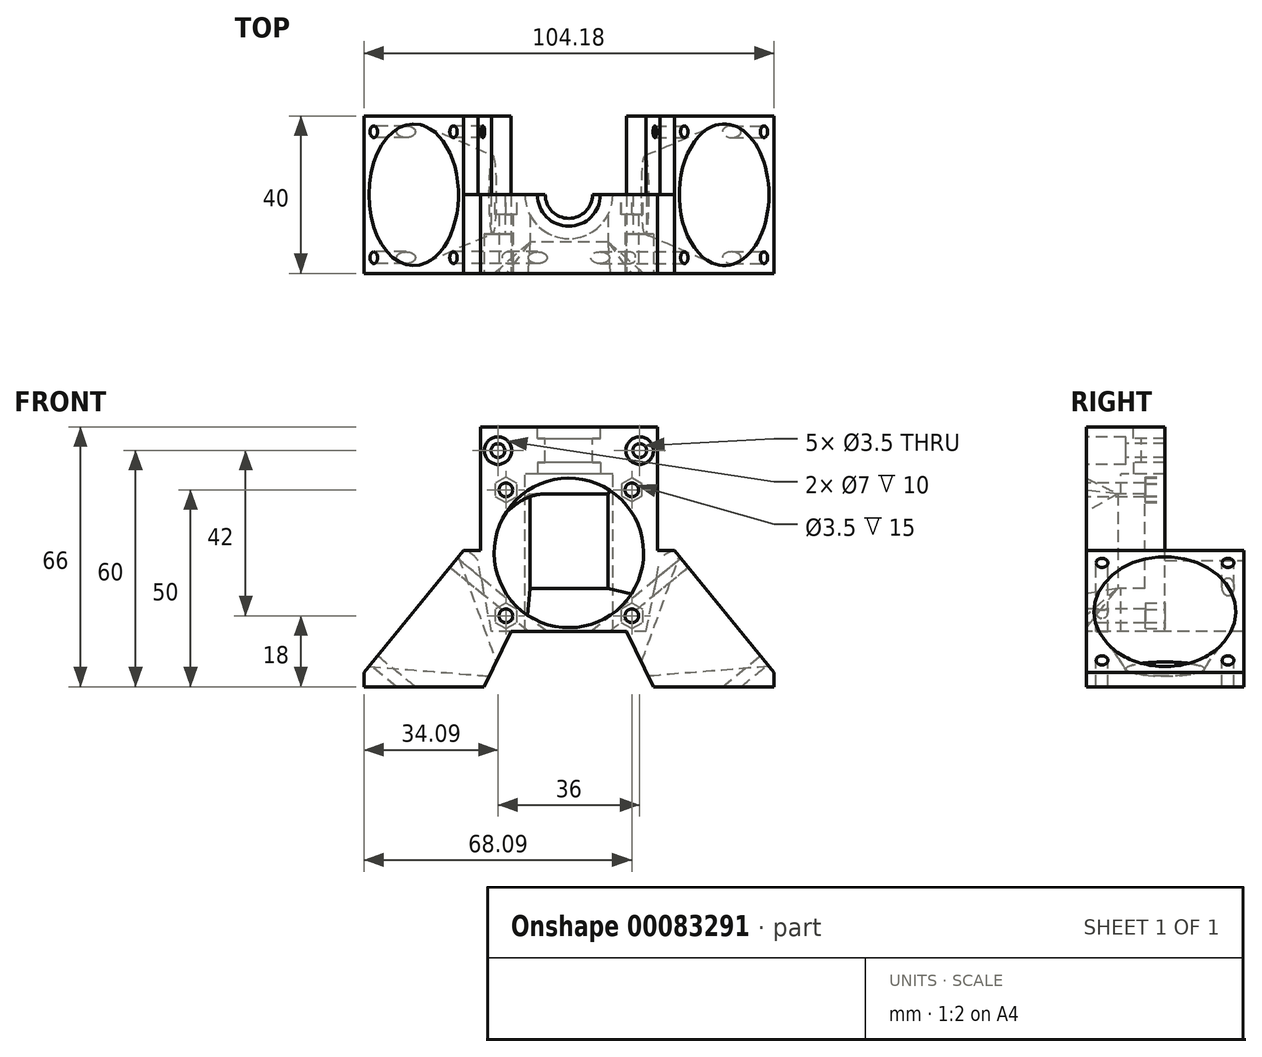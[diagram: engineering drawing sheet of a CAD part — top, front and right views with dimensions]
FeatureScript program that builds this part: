
annotation { "Feature Type Name" : "Feature", "Feature Type Description" : "" }
export const myFeature = defineFeature(function(context is Context, id is Id, definition is map)
    precondition{}
    {
        {
            var Q0;
            Q0=qCreatedBy(makeId("Front.planeOp"),FACE);
            var sketch = newSketch(context, id + "F0", { "sketchPlane" : qUnion([Q0])});
            skLineSegment(sketch, "E0.bottom", {"start": v(22.5, 6) * mm, "end": v(-22.5, 6) * mm});
            skLineSegment(sketch, "E0.top", {"start": v(22.5, -6) * mm, "end": v(-22.5, -6) * mm});
            skLineSegment(sketch, "E0.left", {"start": v(22.5, 6) * mm, "end": v(22.5, -6) * mm});
            skLineSegment(sketch, "E0.right", {"start": v(-22.5, 6) * mm, "end": v(-22.5, -6) * mm});
            skPoint(sketch, "E0.middle", {"position": v(0, 0) * mm});
            skCircle(sketch, "E1", {"center": v(-18, 0) * mm, "radius": 1.75 * mm});
            skCircle(sketch, "E2", {"center": v(-18, 0) * mm, "radius": 3.5 * mm});
            skCircle(sketch, "E3", {"center": v(18, 0) * mm, "radius": 1.75 * mm});
            skCircle(sketch, "E4", {"center": v(18, 0) * mm, "radius": 3.5 * mm});
            skSolve(sketch);
        }
        {
            var Q0;
            Q0=qSketchRegion(id+"F0",true);
            var Q1;
            Q1=makeQuery(id+"F0.imprint","IMPRINT",FACE,{"disambiguationData":[TD([[makeQuery(id+"F0.imprint","IMPRINT",EDGE,{"derivedFrom":sQuery(id+"F0.wireOp",EDGE,"E1")}),-1.0]])]});
            var Q2;
            Q2=makeQuery(id+"F0.imprint","IMPRINT",FACE,{"disambiguationData":[TD([[makeQuery(id+"F0.imprint","IMPRINT",EDGE,{"derivedFrom":sQuery(id+"F0.wireOp",EDGE,"E3")}),-1.0]])]});
            extrude(context, id + "F1", {"entities" : qUnion([Q0, Q1, Q2]), "oppositeDirection" : true, "depth" : 20 * mm});
        }
        {
            var Q0;
            Q0=makeQuery(id+"F0.imprint","IMPRINT",FACE,{"disambiguationData":[TD([[makeQuery(id+"F0.imprint","IMPRINT",EDGE,{"derivedFrom":sQuery(id+"F0.wireOp",EDGE,"E1")}),-1.0]])]});
            var Q1;
            Q1=makeQuery(id+"F0.imprint","IMPRINT",FACE,{"disambiguationData":[TD([[makeQuery(id+"F0.imprint","IMPRINT",EDGE,{"derivedFrom":sQuery(id+"F0.wireOp",EDGE,"E3")}),-1.0]])]});
            extrude(context, id + "F2", {"entities" : qUnion([Q0, Q1]), "operationType" : NewBodyOperationType.REMOVE, "oppositeDirection" : true, "depth" : 10 * mm});
        }
        {
            var Q0;
            Q0=makeQuery(id+"F1.opExtrude","SWEPT_FACE",FACE,{"disambiguationData":[OSD([sQuery(id+"F0.wireOp",EDGE,"E0.bottom")])]});
            var sketch = newSketch(context, id + "F3", { "sketchPlane" : qUnion([Q0])});
            skCircle(sketch, "E5", {"center": v(0, 20) * mm, "radius": 6 * mm});
            skCircle(sketch, "E6", {"center": v(0, 20) * mm, "radius": 8 * mm});
            skSolve(sketch);
        }
        {
            var Q0;
            {var subQ0=sQuery(id+"F3.wireOp",EDGE,"E5");var subQ1=makeQuery(id+"F1.opExtrude","CAP_EDGE",EDGE,{"disambiguationData":[OSD([sQuery(id+"F0.wireOp",EDGE,"E0.bottom")])],"isStart":false});var subQ2=makeQuery(id+"F3.imprint","INTERSECT",VERTEX,{"disambiguationData":[OD(0.0)],"derivedFrom":[subQ1,subQ0]});Q0=makeQuery(id+"F3.imprint","IMPRINT",FACE,{"disambiguationData":[TD([[makeQuery(id+"F3.imprint","IMPRINT",EDGE,{"disambiguationData":[TD([[subQ2,-1.0]])],"derivedFrom":subQ0}),-1.0]])]});}
            var Q1;
            {var subQ0=sQuery(id+"F3.wireOp",EDGE,"E5");var subQ1=makeQuery(id+"F1.opExtrude","CAP_EDGE",EDGE,{"disambiguationData":[OSD([sQuery(id+"F0.wireOp",EDGE,"E0.bottom")])],"isStart":false});var subQ2=makeQuery(id+"F3.imprint","INTERSECT",VERTEX,{"disambiguationData":[OD(0.0)],"derivedFrom":[subQ1,subQ0]});Q1=makeQuery(id+"F3.imprint","IMPRINT",FACE,{"disambiguationData":[TD([[makeQuery(id+"F3.imprint","IMPRINT",EDGE,{"disambiguationData":[TD([[subQ2,-1.0]])],"derivedFrom":subQ0}),1.0]])]});}
            var Q2;
            {var subQ0=sQuery(id+"F3.wireOp",EDGE,"E5");var subQ1=makeQuery(id+"F1.opExtrude","CAP_EDGE",EDGE,{"disambiguationData":[OSD([sQuery(id+"F0.wireOp",EDGE,"E0.bottom")])],"isStart":false});var subQ2=makeQuery(id+"F3.imprint","INTERSECT",VERTEX,{"disambiguationData":[OD(0.0)],"derivedFrom":[subQ1,subQ0]});Q2=makeQuery(id+"F3.imprint","IMPRINT",FACE,{"disambiguationData":[TD([[makeQuery(id+"F3.imprint","IMPRINT",EDGE,{"disambiguationData":[TD([[subQ2,1.0]])],"derivedFrom":subQ0}),1.0]])]});}
            extrude(context, id + "F4", {"entities" : qUnion([Q0, Q1, Q2]), "operationType" : NewBodyOperationType.REMOVE, "endBound" : BoundingType.THROUGH_ALL, "oppositeDirection" : true, "depth" : 25 * mm});
        }
        {
            var Q0;
            Q0=qSketchRegion(id+"F3",true);
            extrude(context, id + "F5", {"entities" : qUnion([Q0]), "operationType" : NewBodyOperationType.REMOVE, "oppositeDirection" : true, "depth" : 3 * mm});
        }
        {
            var Q0;
            Q0=makeQuery(id+"F1.opExtrude","SWEPT_FACE",FACE,{"disambiguationData":[OSD([sQuery(id+"F0.wireOp",EDGE,"E0.top")])]});
            var sketch = newSketch(context, id + "F6", { "sketchPlane" : qUnion([Q0])});
            skCircle(sketch, "E7", {"center": v(0, -20) * mm, "radius": 8 * mm});
            skSolve(sketch);
        }
        {
            var Q0;
            Q0=qSketchRegion(id+"F6",true);
            extrude(context, id + "F7", {"entities" : qUnion([Q0]), "operationType" : NewBodyOperationType.REMOVE, "oppositeDirection" : true, "depth" : 3 * mm});
        }
        {
            var Q0;
            {var subQ0=sQuery(id+"F0.wireOp",EDGE,"E0.top");Q0=makeQuery(id+"F6.imprint","IMPRINT",FACE,{"disambiguationData":[TD([[makeQuery(id+"F6.imprint","IMPRINT",EDGE,{"derivedFrom":makeQuery(id+"F1.opExtrude","CAP_EDGE",EDGE,{"disambiguationData":[OSD([subQ0])],"isStart":true})}),1.0]])]});}
            var sketch = newSketch(context, id + "F8", { "sketchPlane" : qUnion([Q0])});
            skLineSegment(sketch, "E8.bottom", {"start": v(-22.5, 0) * mm, "end": v(22.5, 0) * mm});
            skLineSegment(sketch, "E8.top", {"start": v(-22.5, -20) * mm, "end": v(-11.15, -20) * mm});
            skLineSegment(sketch, "E8.left", {"start": v(-22.5, 0) * mm, "end": v(-22.5, -20) * mm});
            skLineSegment(sketch, "E8.right", {"start": v(22.5, 0) * mm, "end": v(22.5, -20) * mm});
            skArc(sketch, "E9", {"start": v(11.15, -20) * mm, "mid": v(0, -8.85) * mm, "end": v(-11.15, -20) * mm});
            skLineSegment(sketch, "E10.trimOffspring", {"start": v(11.15, -20) * mm, "end": v(22.5, -20) * mm});
            skSolve(sketch);
        }
        {
            var Q0;
            Q0 = qSketchRegion(id + "F8", true);
            extrude(context, id + "F9", {"entities" : qUnion([Q0]), "operationType" : NewBodyOperationType.ADD, "depth" : 40 * mm});
        }
        {
            var Q0;
            Q0=makeQuery(id+"F9.boolean.opBoolean","MERGE",FACE,{"derivedFrom":[makeQuery(id+"F1.opExtrude","CAP_FACE",FACE,{"disambiguationData":[OSD([sQuery(id+"F0.wireOp",EDGE,"E0.bottom"),sQuery(id+"F0.wireOp",EDGE,"E0.top"),sQuery(id+"F0.wireOp",EDGE,"E0.left"),sQuery(id+"F0.wireOp",EDGE,"E0.right"),sQuery(id+"F0.wireOp",EDGE,"E1"),sQuery(id+"F0.wireOp",EDGE,"E3")])],"isStart":true}),makeQuery(id+"F9.opExtrude","SWEPT_FACE",FACE,{"disambiguationData":[OSD([sQuery(id+"F8.wireOp",EDGE,"E8.bottom")])]})]});
            cPlane(context, id + "F10", {"entities" : qUnion([Q0]), "cplaneType" : CPlaneType.OFFSET, "offset" : 8 * mm, "oppositeDirection" : true, "width" : 150 * mm, "height" : 150 * mm});
        }
        {
            var Q0;
            Q0=qCreatedBy(id+"F10.planeOp",FACE);
            var sketch = newSketch(context, id + "F11", { "sketchPlane" : qUnion([Q0])});
            skLineSegment(sketch, "E11.bottom", {"start": v(9.89, -11) * mm, "end": v(-9.89, -11) * mm});
            skLineSegment(sketch, "E11.top", {"start": v(9.89, -35) * mm, "end": v(-9.89, -35) * mm});
            skLineSegment(sketch, "E11.left", {"start": v(9.89, -11) * mm, "end": v(9.89, -35) * mm});
            skLineSegment(sketch, "E11.right", {"start": v(-9.89, -11) * mm, "end": v(-9.89, -35) * mm});
            skPoint(sketch, "E11.middle", {"position": v(0, -23) * mm});
            skSolve(sketch);
        }
        {
            var Q0;
            Q0=makeQuery(id+"F9.boolean.opBoolean","MERGE",FACE,{"derivedFrom":[makeQuery(id+"F1.opExtrude","CAP_FACE",FACE,{"disambiguationData":[OSD([sQuery(id+"F0.wireOp",EDGE,"E0.bottom"),sQuery(id+"F0.wireOp",EDGE,"E0.top"),sQuery(id+"F0.wireOp",EDGE,"E0.left"),sQuery(id+"F0.wireOp",EDGE,"E0.right"),sQuery(id+"F0.wireOp",EDGE,"E1"),sQuery(id+"F0.wireOp",EDGE,"E3")])],"isStart":true}),makeQuery(id+"F9.opExtrude","SWEPT_FACE",FACE,{"disambiguationData":[OSD([sQuery(id+"F8.wireOp",EDGE,"E8.bottom")])]})]});
            var sketch = newSketch(context, id + "F12", { "sketchPlane" : qUnion([Q0])});
            skCircle(sketch, "E12", {"center": v(0, -26) * mm, "radius": 19 * mm});
            skSolve(sketch);
        }
        {
            var Q1;
            Q1 = qSketchRegion(id + "F11", true);
            var Q2;
            Q2 = qSketchRegion(id + "F12", true);
            loft(context, id + "F13", {"operationType" : NewBodyOperationType.REMOVE, "sheetProfilesArray" : [{ "sheetProfileEntities" : qUnion([Q1]) }, { "sheetProfileEntities" : qUnion([Q2]) }]});
        }
        {
            var Q0;
            Q0 = qSketchRegion(id + "F11", true);
            extrude(context, id + "F14", {"entities" : qUnion([Q0]), "operationType" : NewBodyOperationType.REMOVE, "endBound" : BoundingType.THROUGH_ALL, "oppositeDirection" : true, "depth" : 25 * mm});
        }
        {
            var Q0;
            Q0=makeQuery(id+"F9.boolean.opBoolean","MERGE",FACE,{"derivedFrom":[makeQuery(id+"F1.opExtrude","CAP_FACE",FACE,{"disambiguationData":[OSD([sQuery(id+"F0.wireOp",EDGE,"E0.bottom"),sQuery(id+"F0.wireOp",EDGE,"E0.top"),sQuery(id+"F0.wireOp",EDGE,"E0.left"),sQuery(id+"F0.wireOp",EDGE,"E0.right"),sQuery(id+"F0.wireOp",EDGE,"E1"),sQuery(id+"F0.wireOp",EDGE,"E3")])],"isStart":true}),makeQuery(id+"F9.opExtrude","SWEPT_FACE",FACE,{"disambiguationData":[OSD([sQuery(id+"F8.wireOp",EDGE,"E8.bottom")])]})]});
            var sketch = newSketch(context, id + "F15", { "sketchPlane" : qUnion([Q0])});
            skLineSegment(sketch, "E13.bottom", {"start": v(16, -10) * mm, "end": v(-16, -10) * mm, "construction": true});
            skLineSegment(sketch, "E13.top", {"start": v(16, -42) * mm, "end": v(-16, -42) * mm, "construction": true});
            skLineSegment(sketch, "E13.left", {"start": v(16, -10) * mm, "end": v(16, -42) * mm, "construction": true});
            skLineSegment(sketch, "E13.right", {"start": v(-16, -10) * mm, "end": v(-16, -42) * mm, "construction": true});
            skPoint(sketch, "E13.middle", {"position": v(0, -26) * mm});
            skCircle(sketch, "E14", {"center": v(16, -10) * mm, "radius": 1.75 * mm});
            skCircle(sketch, "E15", {"center": v(-16, -10) * mm, "radius": 1.75 * mm});
            skCircle(sketch, "E16", {"center": v(-16, -42) * mm, "radius": 1.75 * mm});
            skCircle(sketch, "E17", {"center": v(16, -42) * mm, "radius": 1.75 * mm});
            skSolve(sketch);
        }
        {
            var Q0;
            Q0 = qSketchRegion(id + "F15", true);
            extrude(context, id + "F16", {"entities" : qUnion([Q0]), "operationType" : NewBodyOperationType.REMOVE, "endBound" : BoundingType.THROUGH_ALL, "oppositeDirection" : true, "depth" : 25 * mm});
        }
        {
            var Q0;
            Q0=qCreatedBy(makeId("Front.planeOp"),FACE);
            var sketch = newSketch(context, id + "F17", { "sketchPlane" : qUnion([Q0])});
            skPoint(sketch, "E18", {"position": v(0, -65) * mm});
            skLineSegment(sketch, "E19", {"start": v(0, -65) * mm, "end": v(-29.37, -50.6) * mm, "construction": true});
            skLineSegment(sketch, "E20", {"start": v(-52.1, -56.41) * mm, "end": v(-52.1, -60) * mm});
            skLineSegment(sketch, "E21", {"start": v(-52.1, -60) * mm, "end": v(-21.55, -60) * mm});
            skLineSegment(sketch, "E22", {"start": v(-21.55, -60) * mm, "end": v(-14.69, -46) * mm});
            skLineSegment(sketch, "E23", {"start": v(-22.5, -25.43) * mm, "end": v(-26.79, -25.43) * mm});
            skLineSegment(sketch, "E24", {"start": v(-26.79, -25.43) * mm, "end": v(-52.1, -56.41) * mm});
            skPoint(sketch, "E25", {"position": v(-14.69, -57.8) * mm});
            skLineSegment(sketch, "E26", {"start": v(-22.5, -46) * mm, "end": v(-22.5, -25.43) * mm});
            skLineSegment(sketch, "E27", {"start": v(-14.69, -46) * mm, "end": v(-22.5, -46) * mm});
            skLineSegment(sketch, "E28", {"start": v(0, 42.58) * mm, "end": v(0, -74.7) * mm, "construction": true});
            skLineSegment(sketch, "E29.MirrorCS", {"start": v(52.1, -56.41) * mm, "end": v(52.1, -60) * mm});
            skLineSegment(sketch, "E30.MirrorCS", {"start": v(22.5, -25.43) * mm, "end": v(26.79, -25.43) * mm});
            skLineSegment(sketch, "E31.MirrorCS", {"start": v(0, -65) * mm, "end": v(29.37, -50.6) * mm, "construction": true});
            skLineSegment(sketch, "E32.MirrorCS", {"start": v(21.55, -60) * mm, "end": v(14.69, -46) * mm});
            skPoint(sketch, "E33.MirrorP", {"position": v(14.69, -57.8) * mm});
            skLineSegment(sketch, "E34.MirrorCS", {"start": v(52.1, -60) * mm, "end": v(21.55, -60) * mm});
            skLineSegment(sketch, "E35.MirrorCS", {"start": v(14.69, -46) * mm, "end": v(22.5, -46) * mm});
            skLineSegment(sketch, "E36.MirrorCS", {"start": v(22.5, -46) * mm, "end": v(22.5, -25.43) * mm});
            skLineSegment(sketch, "E37.MirrorCS", {"start": v(26.79, -25.43) * mm, "end": v(52.1, -56.41) * mm});
            skSolve(sketch);
        }
        {
            var Q0;
            Q0=makeQuery(id+"F17.imprint","IMPRINT",FACE,{"disambiguationData":[TD([[makeQuery(id+"F17.imprint","IMPRINT",EDGE,{"derivedFrom":sQuery(id+"F17.wireOp",EDGE,"f7ET7okq-i3aG-xWv0-ujYL-7c9q7adUJRvd")}),1.0]])]});
            var Q1;
            Q1=makeQuery(id+"F17.imprint","IMPRINT",FACE,{"disambiguationData":[TD([[makeQuery(id+"F17.imprint","IMPRINT",EDGE,{"derivedFrom":sQuery(id+"F17.wireOp",EDGE,"E20")}),1.0]])]});
            var Q2;
            Q2=makeQuery(id+"F17.imprint","IMPRINT",FACE,{"disambiguationData":[TD([[makeQuery(id+"F17.imprint","IMPRINT",EDGE,{"derivedFrom":sQuery(id+"F17.wireOp",EDGE,"E29.MirrorCS")}),-1.0]])]});
            extrude(context, id + "F18", {"entities" : qUnion([Q0, Q1, Q2]), "operationType" : NewBodyOperationType.ADD, "oppositeDirection" : true, "depth" : 40 * mm});
        }
        {
            var Q0;
            Q0=makeQuery(id+"F18.opExtrude","SWEPT_FACE",FACE,{"disambiguationData":[OSD([sQuery(id+"F17.wireOp",EDGE,"E24")])]});
            var sketch = newSketch(context, id + "F19", { "sketchPlane" : qUnion([Q0])});
            skCircle(sketch, "E38", {"center": v(-20, -56.64) * mm, "radius": 18 * mm});
            skSolve(sketch);
        }
        {
            var Q0;
            Q0=makeQuery(id+"F18.opExtrude","SWEPT_FACE",FACE,{"disambiguationData":[OSD([sQuery(id+"F17.wireOp",EDGE,"E22")])]});
            var sketch = newSketch(context, id + "F20", { "sketchPlane" : qUnion([Q0])});
            skEllipse(sketch, "E39", {"center": v(20, -58.36) * mm, "majorRadius": 10 * mm, "minorRadius": 2 * mm, "majorAxis": v(1, 0)});
            skSolve(sketch);
        }
        {
            var Q1;
            Q1=makeQuery(id+"F20.imprint","IMPRINT",FACE,{"disambiguationData":[TD([[makeQuery(id+"F20.imprint","IMPRINT",EDGE,{"derivedFrom":sQuery(id+"F20.wireOp",EDGE,"E39")}),1.0]])]});
            var Q2;
            Q2=makeQuery(id+"F19.imprint","IMPRINT",FACE,{"disambiguationData":[TD([[makeQuery(id+"F19.imprint","IMPRINT",EDGE,{"derivedFrom":sQuery(id+"F19.wireOp",EDGE,"E38")}),1.0]])]});
            loft(context, id + "F21", {"operationType" : NewBodyOperationType.REMOVE, "sheetProfilesArray" : [{ "sheetProfileEntities" : qUnion([Q1]) }, { "sheetProfileEntities" : qUnion([Q2]) }]});
        }
        {
            var Q0;
            {var subQ0=sQuery(id+"F0.wireOp",EDGE,"E3");var subQ1=sQuery(id+"F0.wireOp",EDGE,"E0.left");var subQ2=sQuery(id+"F0.wireOp",EDGE,"E0.top");var subQ3=sQuery(id+"F0.wireOp",EDGE,"E0.bottom");Q0=makeQuery(id+"F9.boolean.opBoolean","MERGE",FACE,{"derivedFrom":[makeQuery(id+"F4.boolean.opBoolean","SPLIT",FACE,{"disambiguationData":[TD([makeQuery(id+"F1.opExtrude","SWEPT_FACE",FACE,{"disambiguationData":[OSD([subQ1])]})])],"derivedFrom":makeQuery(id+"F1.opExtrude","CAP_FACE",FACE,{"disambiguationData":[OSD([subQ3,subQ2,subQ1,sQuery(id+"F0.wireOp",EDGE,"E0.right"),sQuery(id+"F0.wireOp",EDGE,"E1"),subQ0])],"isStart":false})}),makeQuery(id+"F9.opExtrude","SWEPT_FACE",FACE,{"disambiguationData":[OSD([sQuery(id+"F8.wireOp",EDGE,"E10.trimOffspring")])]})]});}
            var sketch = newSketch(context, id + "F22", { "sketchPlane" : qUnion([Q0])});
            skCircle(sketch, "E40.cCircle", {"center": v(16, -10) * mm, "radius": 3.25 * mm, "construction": true});
            skLineSegment(sketch, "E40.0", {"start": v(13.19, -8.38) * mm, "end": v(16, -6.75) * mm});
            skLineSegment(sketch, "E40.1", {"start": v(16, -6.75) * mm, "end": v(18.81, -8.38) * mm});
            skLineSegment(sketch, "E40.2", {"start": v(18.81, -8.38) * mm, "end": v(18.81, -11.63) * mm});
            skLineSegment(sketch, "E40.3", {"start": v(18.81, -11.63) * mm, "end": v(16, -13.25) * mm});
            skLineSegment(sketch, "E40.4", {"start": v(16, -13.25) * mm, "end": v(13.19, -11.62) * mm});
            skLineSegment(sketch, "E40.5", {"start": v(13.19, -11.63) * mm, "end": v(13.19, -8.38) * mm});
            skCircle(sketch, "E41.cCircle", {"center": v(-16, -42) * mm, "radius": 3.25 * mm, "construction": true});
            skLineSegment(sketch, "E41.0", {"start": v(-16, -38.75) * mm, "end": v(-13.19, -40.38) * mm});
            skLineSegment(sketch, "E41.1", {"start": v(-13.19, -40.38) * mm, "end": v(-13.19, -43.63) * mm});
            skLineSegment(sketch, "E41.2", {"start": v(-13.19, -43.63) * mm, "end": v(-16, -45.25) * mm});
            skLineSegment(sketch, "E41.3", {"start": v(-16, -45.25) * mm, "end": v(-18.81, -43.63) * mm});
            skLineSegment(sketch, "E41.4", {"start": v(-18.81, -43.63) * mm, "end": v(-18.81, -40.37) * mm});
            skLineSegment(sketch, "E41.5", {"start": v(-18.81, -40.37) * mm, "end": v(-16, -38.75) * mm});
            skCircle(sketch, "E42.cCircle", {"center": v(-16, -10) * mm, "radius": 3 * mm, "construction": true});
            skLineSegment(sketch, "E42.0", {"start": v(-16, -7) * mm, "end": v(-13.4, -8.5) * mm});
            skLineSegment(sketch, "E42.1", {"start": v(-13.4, -8.5) * mm, "end": v(-13.4, -11.5) * mm});
            skLineSegment(sketch, "E42.2", {"start": v(-13.4, -11.5) * mm, "end": v(-16, -13) * mm});
            skLineSegment(sketch, "E42.3", {"start": v(-16, -13) * mm, "end": v(-18.6, -11.5) * mm});
            skLineSegment(sketch, "E42.4", {"start": v(-18.6, -11.5) * mm, "end": v(-18.6, -8.5) * mm});
            skLineSegment(sketch, "E42.5", {"start": v(-18.6, -8.5) * mm, "end": v(-16, -7) * mm});
            skCircle(sketch, "E43.cCircle", {"center": v(16, -42) * mm, "radius": 3.25 * mm, "construction": true});
            skLineSegment(sketch, "E43.0", {"start": v(16, -38.75) * mm, "end": v(18.81, -40.38) * mm});
            skLineSegment(sketch, "E43.1", {"start": v(18.81, -40.38) * mm, "end": v(18.81, -43.63) * mm});
            skLineSegment(sketch, "E43.2", {"start": v(18.81, -43.63) * mm, "end": v(16, -45.25) * mm});
            skLineSegment(sketch, "E43.3", {"start": v(16, -45.25) * mm, "end": v(13.19, -43.63) * mm});
            skLineSegment(sketch, "E43.4", {"start": v(13.19, -43.63) * mm, "end": v(13.19, -40.38) * mm});
            skLineSegment(sketch, "E43.5", {"start": v(13.19, -40.38) * mm, "end": v(16, -38.75) * mm});
            skSolve(sketch);
        }
        {
            var Q0;
            Q0 = qSketchRegion(id + "F22", true);
            extrude(context, id + "F23", {"entities" : qUnion([Q0]), "operationType" : NewBodyOperationType.REMOVE, "oppositeDirection" : true, "depth" : 5 * mm});
        }
        {
            var Q0;
            Q0=makeQuery(id+"F18.opExtrude","SWEPT_FACE",FACE,{"disambiguationData":[OSD([sQuery(id+"F17.wireOp",EDGE,"E37.MirrorCS")])]});
            var sketch = newSketch(context, id + "F24", { "sketchPlane" : qUnion([Q0])});
            skCircle(sketch, "E44", {"center": v(20, -56.64) * mm, "radius": 18 * mm});
            skSolve(sketch);
        }
        {
            var Q0;
            Q0=makeQuery(id+"F18.opExtrude","SWEPT_FACE",FACE,{"disambiguationData":[OSD([sQuery(id+"F17.wireOp",EDGE,"E32.MirrorCS")])]});
            var sketch = newSketch(context, id + "F25", { "sketchPlane" : qUnion([Q0])});
            skEllipse(sketch, "E45", {"center": v(-20, -58.36) * mm, "majorRadius": 10 * mm, "minorRadius": 2 * mm, "majorAxis": v(1, 0)});
            skSolve(sketch);
        }
        {
            var Q1;
            Q1=makeQuery(id+"F24.imprint","IMPRINT",FACE,{"disambiguationData":[TD([[makeQuery(id+"F24.imprint","IMPRINT",EDGE,{"derivedFrom":sQuery(id+"F24.wireOp",EDGE,"E44")}),1.0]])]});
            var Q2;
            Q2=makeQuery(id+"F25.imprint","IMPRINT",FACE,{"disambiguationData":[TD([[makeQuery(id+"F25.imprint","IMPRINT",EDGE,{"derivedFrom":sQuery(id+"F25.wireOp",EDGE,"E45")}),1.0]])]});
            loft(context, id + "F26", {"operationType" : NewBodyOperationType.REMOVE, "sheetProfilesArray" : [{ "sheetProfileEntities" : qUnion([Q1]) }, { "sheetProfileEntities" : qUnion([Q2]) }]});
        }
        {
            var Q0;
            {var subQ0=sQuery(id+"F17.wireOp",EDGE,"E23");Q0=makeQuery(id+"F18.boolean.opBoolean","SPLIT",EDGE,{"disambiguationData":[topologyDisambiguationEdgeConnected([makeQuery(id+"F1.opExtrude","SWEPT_FACE",FACE,{"disambiguationData":[OSD([sQuery(id+"F0.wireOp",EDGE,"E0.right")])]})])],"derivedFrom":makeQuery(id+"F18.opExtrude","SWEPT_EDGE",EDGE,{"disambiguationData":[OSD([subQ0,sQuery(id+"F17.wireOp",EDGE,"E26")])]})});}
            var Q1;
            {var subQ0=sQuery(id+"F17.wireOp",EDGE,"E30.MirrorCS");Q1=makeQuery(id+"F18.boolean.opBoolean","SPLIT",EDGE,{"disambiguationData":[topologyDisambiguationEdgeConnected([makeQuery(id+"F1.opExtrude","SWEPT_FACE",FACE,{"disambiguationData":[OSD([sQuery(id+"F0.wireOp",EDGE,"E0.left")])]})])],"derivedFrom":makeQuery(id+"F18.opExtrude","SWEPT_EDGE",EDGE,{"disambiguationData":[OSD([subQ0,sQuery(id+"F17.wireOp",EDGE,"E36.MirrorCS")])]})});}
            fillet(context, id + "F27", {"entities" : qUnion([Q0, Q1]), "radius" : 5 * mm, "tangentPropagation" : true, "allowEdgeOverflow" : false});
        }
        {
            var Q0;
            Q0=makeQuery(id+"F19.imprint","IMPRINT",FACE,{"disambiguationData":[TD([[makeQuery(id+"F19.imprint","IMPRINT",EDGE,{"derivedFrom":sQuery(id+"F19.wireOp",EDGE,"E38")}),-1.0]])]});
            var sketch = newSketch(context, id + "F28", { "sketchPlane" : qUnion([Q0])});
            skLineSegment(sketch, "E46.bottom", {"start": v(-4, -72.64) * mm, "end": v(-36, -72.64) * mm, "construction": true});
            skLineSegment(sketch, "E46.top", {"start": v(-4, -40.64) * mm, "end": v(-36, -40.64) * mm, "construction": true});
            skLineSegment(sketch, "E46.left", {"start": v(-4, -72.64) * mm, "end": v(-4, -40.64) * mm, "construction": true});
            skLineSegment(sketch, "E46.right", {"start": v(-36, -72.64) * mm, "end": v(-36, -40.64) * mm, "construction": true});
            skPoint(sketch, "E46.middle", {"position": v(-20, -56.64) * mm});
            skCircle(sketch, "E47", {"center": v(-36, -72.64) * mm, "radius": 1.5 * mm});
            skCircle(sketch, "E48", {"center": v(-4, -72.64) * mm, "radius": 1.5 * mm});
            skCircle(sketch, "E49", {"center": v(-4, -40.64) * mm, "radius": 1.5 * mm});
            skCircle(sketch, "E50", {"center": v(-36, -40.64) * mm, "radius": 1.5 * mm});
            skSolve(sketch);
        }
        {
            var Q0;
            Q0 = qSketchRegion(id + "F28", true);
            extrude(context, id + "F29", {"entities" : qUnion([Q0]), "operationType" : NewBodyOperationType.REMOVE, "endBound" : BoundingType.THROUGH_ALL, "oppositeDirection" : true, "depth" : 25 * mm});
        }
        {
            var Q0;
            Q0=makeQuery(id+"F18.opExtrude","SWEPT_FACE",FACE,{"disambiguationData":[OSD([sQuery(id+"F17.wireOp",EDGE,"E37.MirrorCS")])]});
            var sketch = newSketch(context, id + "F30", { "sketchPlane" : qUnion([Q0])});
            skLineSegment(sketch, "E51.bottom", {"start": v(36, -72.64) * mm, "end": v(4, -72.64) * mm, "construction": true});
            skLineSegment(sketch, "E51.top", {"start": v(36, -40.64) * mm, "end": v(4, -40.64) * mm, "construction": true});
            skLineSegment(sketch, "E51.left", {"start": v(36, -72.64) * mm, "end": v(36, -40.64) * mm, "construction": true});
            skLineSegment(sketch, "E51.right", {"start": v(4, -72.64) * mm, "end": v(4, -40.64) * mm, "construction": true});
            skPoint(sketch, "E51.middle", {"position": v(20, -56.64) * mm});
            skCircle(sketch, "E52", {"center": v(4, -72.64) * mm, "radius": 1.5 * mm});
            skCircle(sketch, "E53", {"center": v(36, -72.64) * mm, "radius": 1.5 * mm});
            skCircle(sketch, "E54", {"center": v(36, -40.64) * mm, "radius": 1.5 * mm});
            skCircle(sketch, "E55", {"center": v(4, -40.64) * mm, "radius": 1.5 * mm});
            skSolve(sketch);
        }
        {
            var Q0;
            Q0 = qSketchRegion(id + "F30", true);
            extrude(context, id + "F31", {"entities" : qUnion([Q0]), "operationType" : NewBodyOperationType.REMOVE, "endBound" : BoundingType.THROUGH_ALL, "oppositeDirection" : true, "depth" : 25 * mm});
        }
        {
            var Q0;
            Q0=makeQuery(id+"F18.opExtrude","SWEPT_EDGE",EDGE,{"disambiguationData":[OSD([sQuery(id+"F17.wireOp",EDGE,"E35.MirrorCS"),sQuery(id+"F17.wireOp",EDGE,"E36.MirrorCS")])]});
            chamfer(context, id + "F32", {"entities" : qUnion([Q0]), "chamferType" : ChamferType.TWO_OFFSETS, "width1" : 20 * mm, "oppositeDirection" : false, "width2" : 4 * mm, "tangentPropagation" : true});
        }
        {
            var Q0;
            Q0=makeQuery(id+"F18.opExtrude","SWEPT_EDGE",EDGE,{"disambiguationData":[OSD([sQuery(id+"F17.wireOp",EDGE,"E26"),sQuery(id+"F17.wireOp",EDGE,"E27")])]});
            chamfer(context, id + "F33", {"entities" : qUnion([Q0]), "chamferType" : ChamferType.TWO_OFFSETS, "width1" : 4 * mm, "oppositeDirection" : false, "width2" : 20 * mm, "tangentPropagation" : true});
        }
    });
